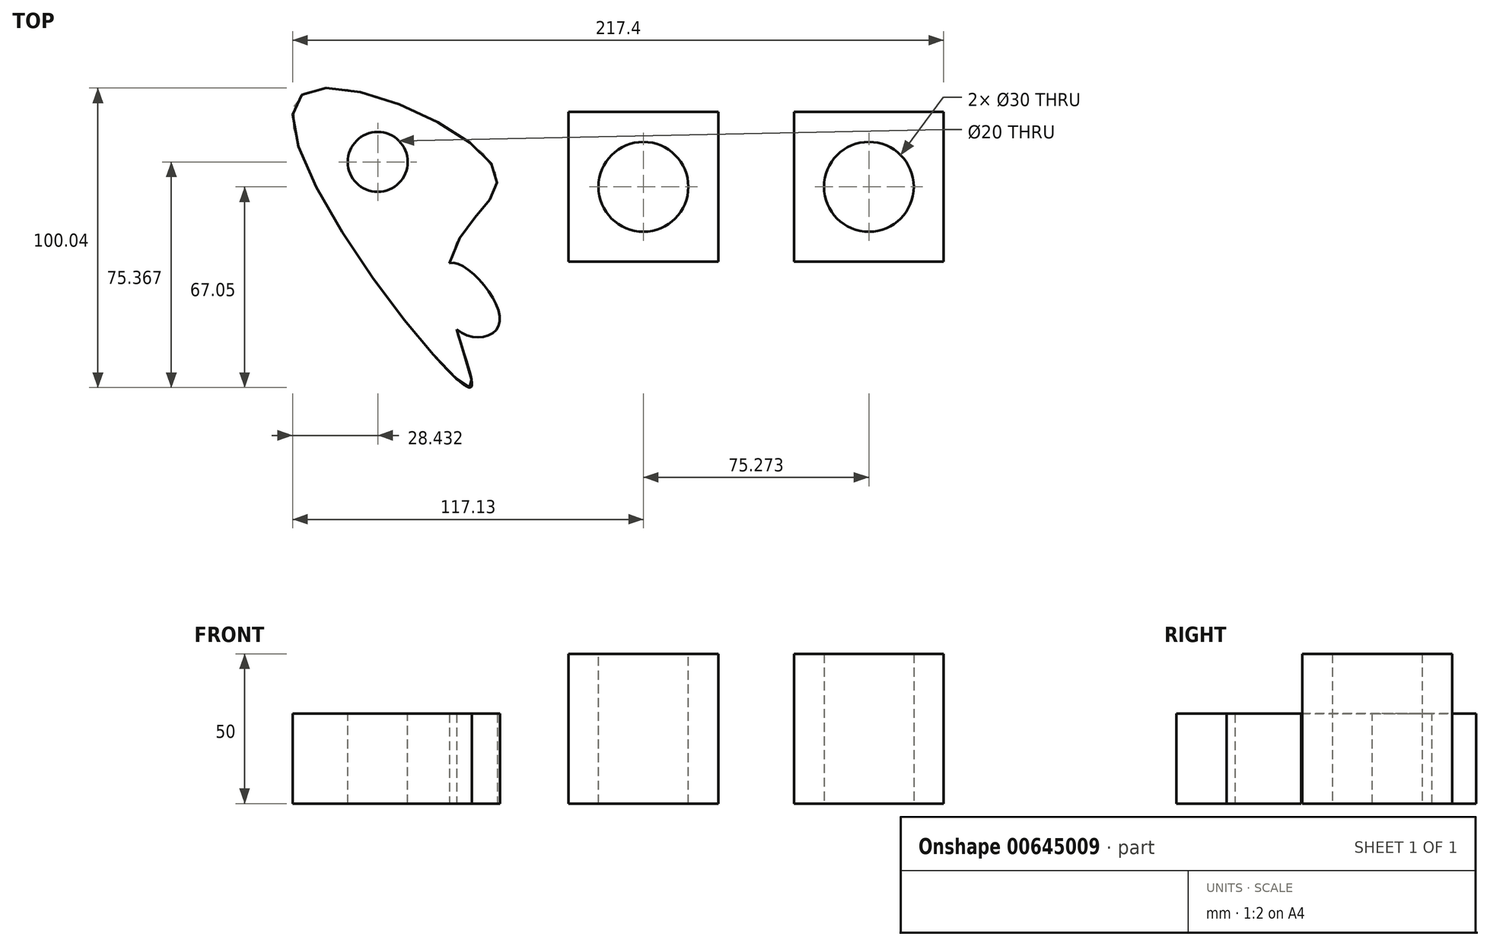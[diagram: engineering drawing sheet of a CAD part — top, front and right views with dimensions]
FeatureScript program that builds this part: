
annotation { "Feature Type Name" : "Feature", "Feature Type Description" : "" }
export const myFeature = defineFeature(function(context is Context, id is Id, definition is map)
    precondition{}
    {
        {
            var Q0;
            Q0=qCreatedBy(makeId("Top.planeOp"),FACE);
            var sketch = newSketch(context, id + "F0", { "sketchPlane" : qUnion([Q0])});
            skLineSegment(sketch, "E0.bottom", {"start": v(-25, -25) * mm, "end": v(25, -25) * mm});
            skLineSegment(sketch, "E0.top", {"start": v(-25, 25) * mm, "end": v(25, 25) * mm});
            skLineSegment(sketch, "E0.left", {"start": v(-25, -25) * mm, "end": v(-25, 25) * mm});
            skLineSegment(sketch, "E0.right", {"start": v(25, -25) * mm, "end": v(25, 25) * mm});
            skPoint(sketch, "E0.middle", {"position": v(0, 0) * mm});
            skSolve(sketch);
        }
        {
            var Q0;
            Q0 = qSketchRegion(id + "F0", true);
            extrude(context, id + "F1", {"entities" : qUnion([Q0]), "depth" : 50 * mm, "offsetDistance" : 25 * mm});
        }
        {
            var Q0;
            Q0=makeQuery(id+"F1.opExtrude","CAP_FACE",FACE,{"disambiguationData":[OSD([sQuery(id+"F0.wireOp",EDGE,"E0.bottom"),sQuery(id+"F0.wireOp",EDGE,"E0.top"),sQuery(id+"F0.wireOp",EDGE,"E0.left"),sQuery(id+"F0.wireOp",EDGE,"E0.right")])],"isStart":false});
            var sketch = newSketch(context, id + "F2", { "sketchPlane" : qUnion([Q0])});
            skCircle(sketch, "E1", {"center": v(0, 0) * mm, "radius": 15 * mm});
            skSolve(sketch);
        }
        {
            var Q0;
            Q0 = qSketchRegion(id + "F2", true);
            extrude(context, id + "F3", {"entities" : qUnion([Q0]), "operationType" : NewBodyOperationType.REMOVE, "oppositeDirection" : true, "depth" : 50 * mm, "offsetDistance" : 25 * mm});
        }
        {
            var Q0;
            Q0=qCreatedBy(makeId("Top.planeOp"),FACE);
            var sketch = newSketch(context, id + "F4", { "sketchPlane" : qUnion([Q0])});
            skLineSegment(sketch, "E2.bottom", {"start": v(50.27, 25) * mm, "end": v(100.27, 25) * mm});
            skLineSegment(sketch, "E2.top", {"start": v(50.27, -25) * mm, "end": v(100.27, -25) * mm});
            skLineSegment(sketch, "E2.left", {"start": v(50.27, 25) * mm, "end": v(50.27, -25) * mm});
            skLineSegment(sketch, "E2.right", {"start": v(100.27, 25) * mm, "end": v(100.27, -25) * mm});
            skPoint(sketch, "E2.middle", {"position": v(75.27, 0) * mm});
            skCircle(sketch, "E3", {"center": v(75.27, 0) * mm, "radius": 15 * mm});
            skSolve(sketch);
        }
        {
            var Q0;
            Q0 = qSketchRegion(id + "F4", true);
            extrude(context, id + "F5", {"entities" : qUnion([Q0]), "depth" : 50 * mm, "offsetDistance" : 25 * mm});
        }
        {
            var Q0;
            Q0=qCreatedBy(makeId("Top.planeOp"),FACE);
            var sketch = newSketch(context, id + "F6", { "sketchPlane" : qUnion([Q0])});
            skFitSpline(sketch, "E4", {"points": [v(-64.7, -25.47) * mm, v(-49.67, 5.92) * mm, v(-116.01, 28.47) * mm, v(-58.31, -67) * mm, v(-64.7, -25.47) * mm]});
            skFitSpline(sketch, "E5", {"points": [v(-62.3, -47.56) * mm, v(-47.98, -45.2) * mm, v(-64.7, -25.47) * mm, v(-62.3, -47.56) * mm]});
            skSolve(sketch);
        }
        {
            var Q0;
            Q0 = qSketchRegion(id + "F6", true);
            extrude(context, id + "F7", {"entities" : qUnion([Q0]), "depth" : 30 * mm, "offsetDistance" : 25 * mm});
        }
        {
            var Q0;
            Q0=makeQuery(id+"F7.opExtrude","CAP_FACE",FACE,{"disambiguationData":[OSD([sQuery(id+"F6.wireOp",EDGE,"E4"),sQuery(id+"F6.wireOp",EDGE,"E5")])],"isStart":false});
            var sketch = newSketch(context, id + "F8", { "sketchPlane" : qUnion([Q0])});
            skCircle(sketch, "E6", {"center": v(-88.7, 8.32) * mm, "radius": 10 * mm});
            skSolve(sketch);
        }
        {
            var Q0;
            Q0 = qSketchRegion(id + "F8", true);
            extrude(context, id + "F9", {"entities" : qUnion([Q0]), "operationType" : NewBodyOperationType.REMOVE, "oppositeDirection" : true, "depth" : 30 * mm, "offsetDistance" : 25 * mm});
        }
    });
